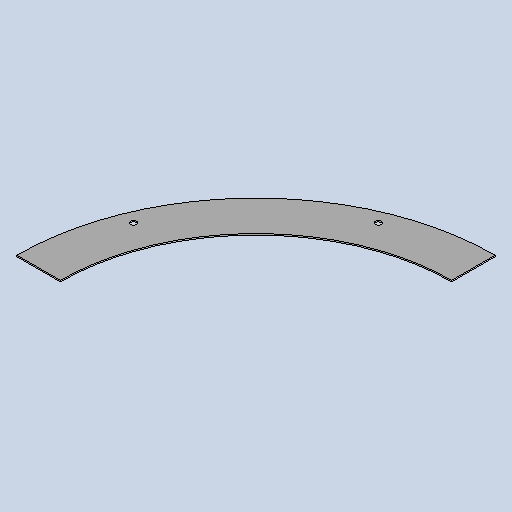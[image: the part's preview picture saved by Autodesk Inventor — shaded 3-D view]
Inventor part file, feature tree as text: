
AUTODESK INVENTOR PART (.ipt)
format: ipt  version: 2025 (Build 290162010, 162A)  size: 130,048 bytes
history: native  units: mm
features: other x3, sketch x2, sheet_metal_op x1, pattern_circular x1
ambient origin geometry x8: Origin, YZ Plane, XZ Plane, XY Plane, X Axis, Y Axis, Z Axis, Center Point
bodies: Solid1 (feature_tree)
feature tree (7):
  sheet_metal_op  "Face1"
  pattern_circular  "Circular Pattern1"  Count=110  [1 undecoded]
  sketch  "Sketch1"  dims[d1=900.0mm]
  other  "Plate1"
  sketch  "Sketch2"  dims[d2=3.0mm d4=14.0mm d6=3.0mm d7=0.0mm d8=20.0mm d9=45.0deg d11=1040.0mm d12=22.5deg]
  other  "Cut1"
  other  "Definition1"
note: 1 required parameter value undecoded (feature->parameter linkage not recoverable at this tier; creation-order binding heuristic only, values carry confidence <= 0.55)
